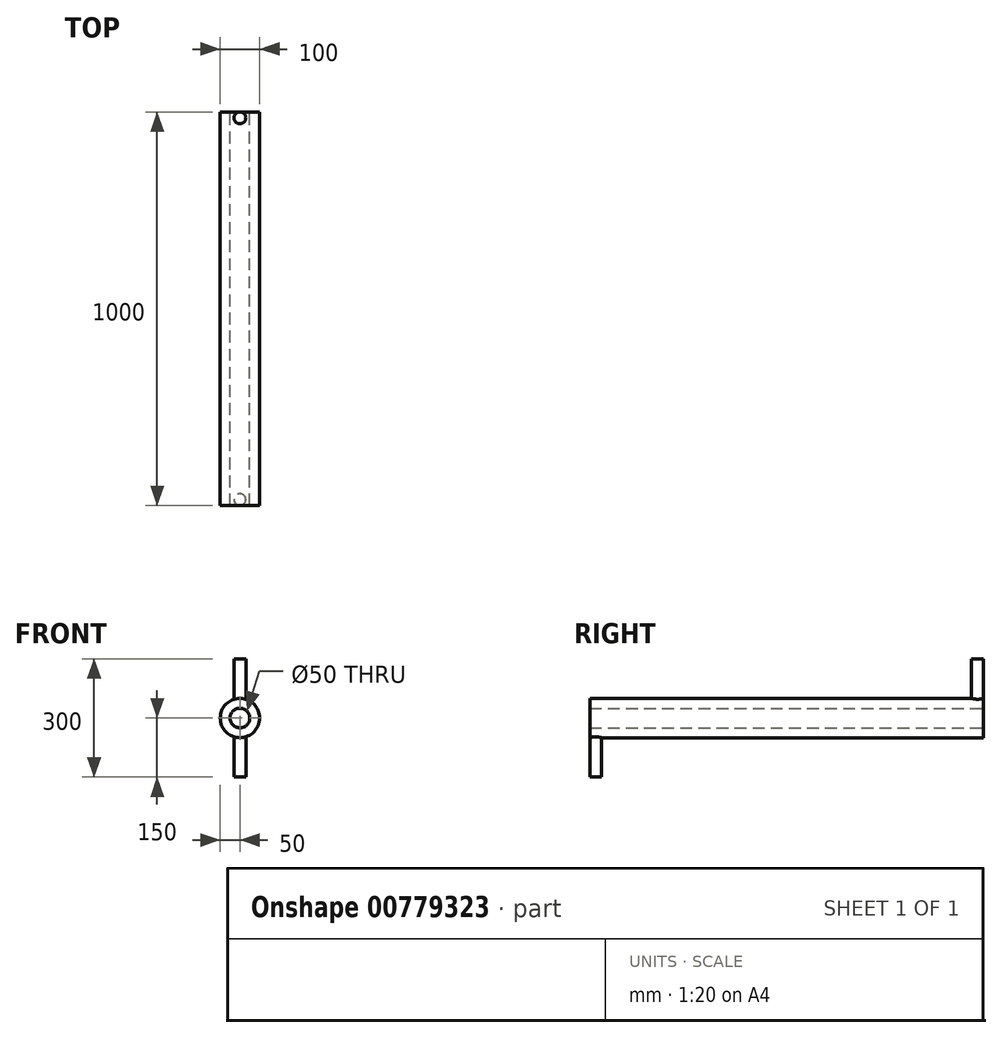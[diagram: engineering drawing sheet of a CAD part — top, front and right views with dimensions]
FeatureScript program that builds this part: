
annotation { "Feature Type Name" : "Feature", "Feature Type Description" : "" }
export const myFeature = defineFeature(function(context is Context, id is Id, definition is map)
    precondition{}
    {
        {
            var Q0;
            Q0=qCreatedBy(makeId("Front.planeOp"),FACE);
            var sketch = newSketch(context, id + "F0", { "sketchPlane" : qUnion([Q0])});
            skCircle(sketch, "E0", {"center": v(0, 0) * mm, "radius": 50 * mm});
            skCircle(sketch, "E1", {"center": v(0, 0) * mm, "radius": 25 * mm});
            skSolve(sketch);
        }
        {
            var Q0;
            Q0=qCreatedBy(makeId("Top.planeOp"),FACE);
            cPlane(context, id + "F1", {"entities" : qUnion([Q0]), "cplaneType" : CPlaneType.OFFSET, "offset" : 25 * mm, "width" : 150 * mm, "height" : 150 * mm});
        }
        {
            var Q0;
            Q0=qCreatedBy(id+"F1.planeOp",FACE);
            var sketch = newSketch(context, id + "F2", { "sketchPlane" : qUnion([Q0])});
            skCircle(sketch, "E2", {"center": v(0, -15) * mm, "radius": 15 * mm});
            skSolve(sketch);
        }
        {
            var Q0;
            Q0=qCreatedBy(makeId("Top.planeOp"),FACE);
            cPlane(context, id + "F3", {"entities" : qUnion([Q0]), "cplaneType" : CPlaneType.OFFSET, "offset" : 25 * mm, "oppositeDirection" : true, "width" : 150 * mm, "height" : 150 * mm});
        }
        {
            var Q0;
            Q0=qCreatedBy(id+"F3.planeOp",FACE);
            var sketch = newSketch(context, id + "F4", { "sketchPlane" : qUnion([Q0])});
            skCircle(sketch, "E3", {"center": v(0, -985) * mm, "radius": 15 * mm});
            skSolve(sketch);
        }
        {
            var Q0;
            Q0=makeQuery(id+"F0.imprint","IMPRINT",FACE,{"disambiguationData":[TD([[makeQuery(id+"F0.imprint","IMPRINT",EDGE,{"derivedFrom":sQuery(id+"F0.wireOp",EDGE,"E0")}),1.0]])]});
            extrude(context, id + "F5", {"entities" : qUnion([Q0]), "depth" : 1000 * mm, "offsetDistance" : 25 * mm});
        }
        {
            var Q0;
            Q0 = qSketchRegion(id + "F2", true);
            extrude(context, id + "F6", {"entities" : qUnion([Q0]), "operationType" : NewBodyOperationType.ADD, "depth" : 125 * mm, "offsetDistance" : 25 * mm});
        }
        {
            var Q0;
            Q0 = qSketchRegion(id + "F4", true);
            extrude(context, id + "F7", {"entities" : qUnion([Q0]), "operationType" : NewBodyOperationType.ADD, "oppositeDirection" : true, "depth" : 125 * mm, "offsetDistance" : 25 * mm});
        }
    });
